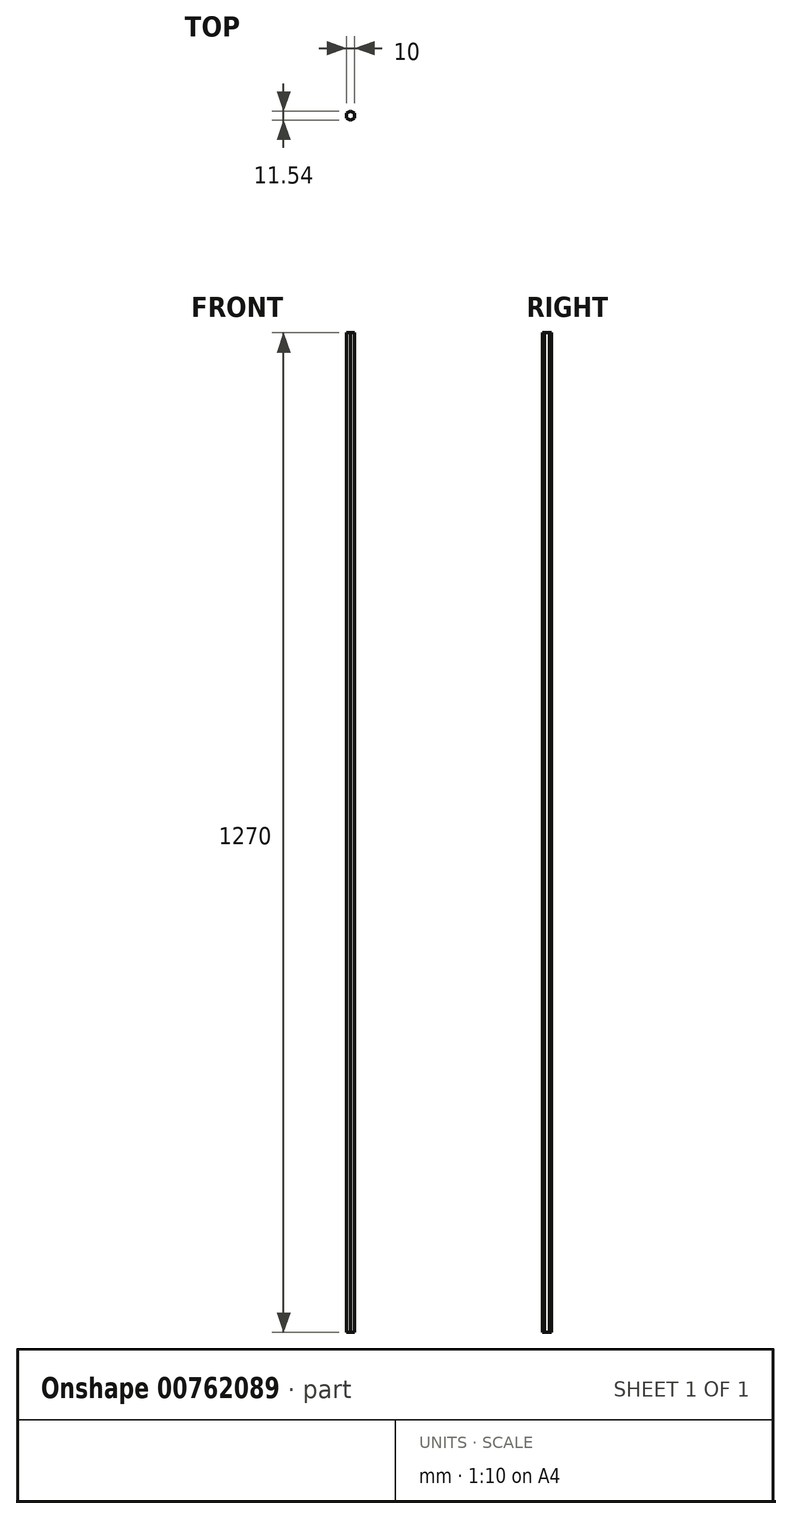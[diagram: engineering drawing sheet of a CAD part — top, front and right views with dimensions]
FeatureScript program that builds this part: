
annotation { "Feature Type Name" : "Feature", "Feature Type Description" : "" }
export const myFeature = defineFeature(function(context is Context, id is Id, definition is map)
    precondition{}
    {
        {
            var Q0;
            Q0=qCreatedBy(makeId("Top.planeOp"),FACE);
            var sketch = newSketch(context, id + "F0", { "sketchPlane" : qUnion([Q0])});
            skCircle(sketch, "E0.cCircle", {"center": v(0, 0) * mm, "radius": 5 * mm, "construction": true});
            skLineSegment(sketch, "E0.0", {"start": v(5, 2.89) * mm, "end": v(5, -2.89) * mm});
            skLineSegment(sketch, "E0.1", {"start": v(5, -2.89) * mm, "end": v(0, -5.77) * mm});
            skLineSegment(sketch, "E0.2", {"start": v(0, -5.77) * mm, "end": v(-5, -2.89) * mm});
            skLineSegment(sketch, "E0.3", {"start": v(-5, -2.89) * mm, "end": v(-5, 2.89) * mm});
            skLineSegment(sketch, "E0.4", {"start": v(-5, 2.89) * mm, "end": v(0, 5.77) * mm});
            skLineSegment(sketch, "E0.5", {"start": v(0, 5.77) * mm, "end": v(5, 2.89) * mm});
            skPoint(sketch, "E0.0.midPoint", {"position": v(5, 0) * mm});
            skSolve(sketch);
        }
        {
            var Q0;
            Q0 = qSketchRegion(id + "F0", true);
            extrude(context, id + "F1", {"entities" : qUnion([Q0]), "depth" : 1270 * mm, "offsetDistance" : 25.4 * mm});
        }
    });
